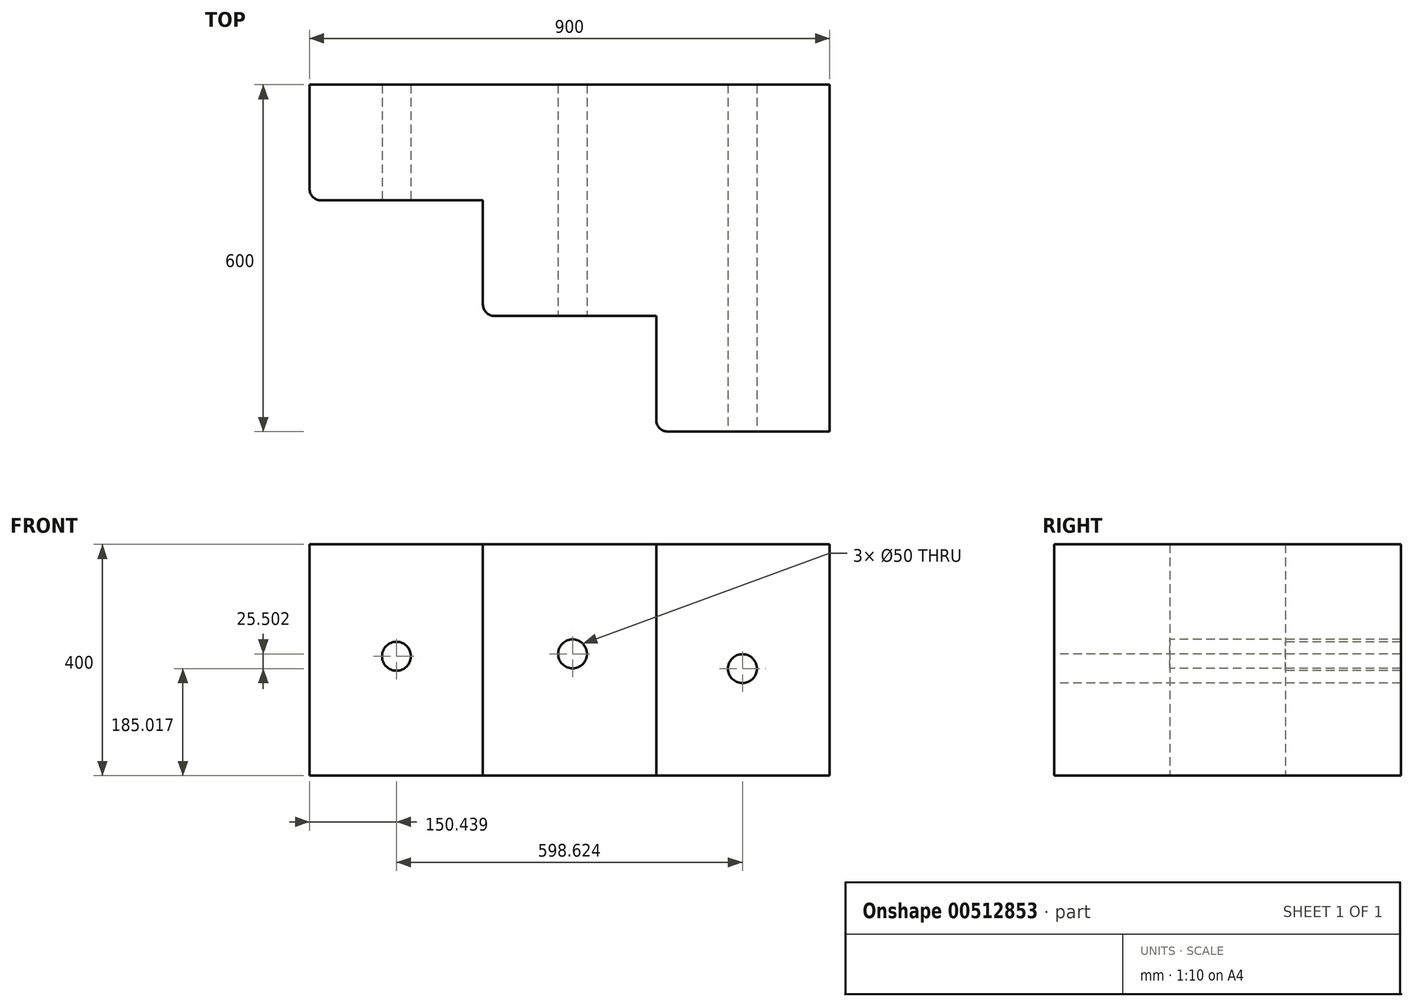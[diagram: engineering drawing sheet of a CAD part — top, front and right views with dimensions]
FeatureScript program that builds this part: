
annotation { "Feature Type Name" : "Feature", "Feature Type Description" : "" }
export const myFeature = defineFeature(function(context is Context, id is Id, definition is map)
    precondition{}
    {
        {
            var Q0;
            Q0=qCreatedBy(makeId("Top.planeOp"),FACE);
            var sketch = newSketch(context, id + "F0", { "sketchPlane" : qUnion([Q0])});
            skLineSegment(sketch, "E0.bottom", {"start": v(0, 0) * mm, "end": v(900, 0) * mm});
            skLineSegment(sketch, "E0.top", {"start": v(600, -600) * mm, "end": v(900, -600) * mm});
            skLineSegment(sketch, "E0.left", {"start": v(0, 0) * mm, "end": v(0, -200) * mm});
            skLineSegment(sketch, "E0.right", {"start": v(900, 0) * mm, "end": v(900, -600) * mm});
            skLineSegment(sketch, "E1", {"start": v(600, -600) * mm, "end": v(600, -400) * mm});
            skLineSegment(sketch, "E2", {"start": v(600, -400) * mm, "end": v(300, -400) * mm});
            skLineSegment(sketch, "E3", {"start": v(300, -400) * mm, "end": v(300, -200) * mm});
            skLineSegment(sketch, "E4", {"start": v(300, -200) * mm, "end": v(0, -200) * mm});
            skSolve(sketch);
        }
        {
            var Q0;
            Q0 = qSketchRegion(id + "F0", true);
            extrude(context, id + "F1", {"entities" : qUnion([Q0]), "depth" : 400 * mm});
        }
        {
            var Q0;
            Q0=makeQuery(id+"F1.opExtrude","SWEPT_EDGE",EDGE,{"disambiguationData":[OSD([sQuery(id+"F0.wireOp",EDGE,"E1"),sQuery(id+"F0.wireOp",EDGE,"E0.top")])]});
            var Q1;
            Q1=makeQuery(id+"F1.opExtrude","SWEPT_EDGE",EDGE,{"disambiguationData":[OSD([sQuery(id+"F0.wireOp",EDGE,"E2"),sQuery(id+"F0.wireOp",EDGE,"E3")])]});
            var Q2;
            Q2=makeQuery(id+"F1.opExtrude","SWEPT_EDGE",EDGE,{"disambiguationData":[OSD([sQuery(id+"F0.wireOp",EDGE,"E0.left"),sQuery(id+"F0.wireOp",EDGE,"E4")])]});
            fillet(context, id + "F2", {"entities" : qUnion([Q0, Q1, Q2]), "radius" : 20 * mm, "tangentPropagation" : true, "allowEdgeOverflow" : false});
        }
        {
            var Q0;
            Q0=makeQuery(id+"F1.opExtrude","SWEPT_FACE",FACE,{"disambiguationData":[OSD([sQuery(id+"F0.wireOp",EDGE,"E4")])]});
            var sketch = newSketch(context, id + "F3", { "sketchPlane" : qUnion([Q0])});
            skSolve(sketch);
        }
        {
            var Q0;
            {var subQ0=sQuery(id+"F0.wireOp",EDGE,"E4");Q0=makeQuery(id+"F3.imprint","IMPRINT",FACE,{"disambiguationData":[TD([[makeQuery(id+"F3.imprint","IMPRINT",EDGE,{"derivedFrom":makeQuery(id+"F1.opExtrude","CAP_EDGE",EDGE,{"disambiguationData":[OSD([subQ0])],"isStart":true})}),-1.0]])]});}
            var sketch = newSketch(context, id + "F4", { "sketchPlane" : qUnion([Q0])});
            skCircle(sketch, "E5", {"center": v(150.44, 206.5) * mm, "radius": 25 * mm});
            skSolve(sketch);
        }
        {
            var Q0;
            Q0 = qSketchRegion(id + "F4", true);
            extrude(context, id + "F5", {"entities" : qUnion([Q0]), "operationType" : NewBodyOperationType.REMOVE, "endBound" : BoundingType.THROUGH_ALL, "oppositeDirection" : true, "depth" : 25.4 * mm});
        }
        {
            var Q0;
            Q0=makeQuery(id+"F1.opExtrude","SWEPT_FACE",FACE,{"disambiguationData":[OSD([sQuery(id+"F0.wireOp",EDGE,"E2")])]});
            var sketch = newSketch(context, id + "F6", { "sketchPlane" : qUnion([Q0])});
            skCircle(sketch, "E6", {"center": v(455.12, 210.52) * mm, "radius": 25 * mm});
            skSolve(sketch);
        }
        {
            var Q0;
            Q0 = qSketchRegion(id + "F6", true);
            extrude(context, id + "F7", {"entities" : qUnion([Q0]), "operationType" : NewBodyOperationType.REMOVE, "endBound" : BoundingType.THROUGH_ALL, "oppositeDirection" : true, "depth" : 25.4 * mm});
        }
        {
            var Q0;
            Q0=makeQuery(id+"F1.opExtrude","SWEPT_FACE",FACE,{"disambiguationData":[OSD([sQuery(id+"F0.wireOp",EDGE,"E0.top")])]});
            var sketch = newSketch(context, id + "F8", { "sketchPlane" : qUnion([Q0])});
            skCircle(sketch, "E7", {"center": v(749.06, 185.02) * mm, "radius": 25 * mm});
            skSolve(sketch);
        }
        {
            var Q0;
            Q0 = qSketchRegion(id + "F8", true);
            extrude(context, id + "F9", {"entities" : qUnion([Q0]), "operationType" : NewBodyOperationType.REMOVE, "endBound" : BoundingType.THROUGH_ALL, "oppositeDirection" : true, "depth" : 25.4 * mm});
        }
    });
